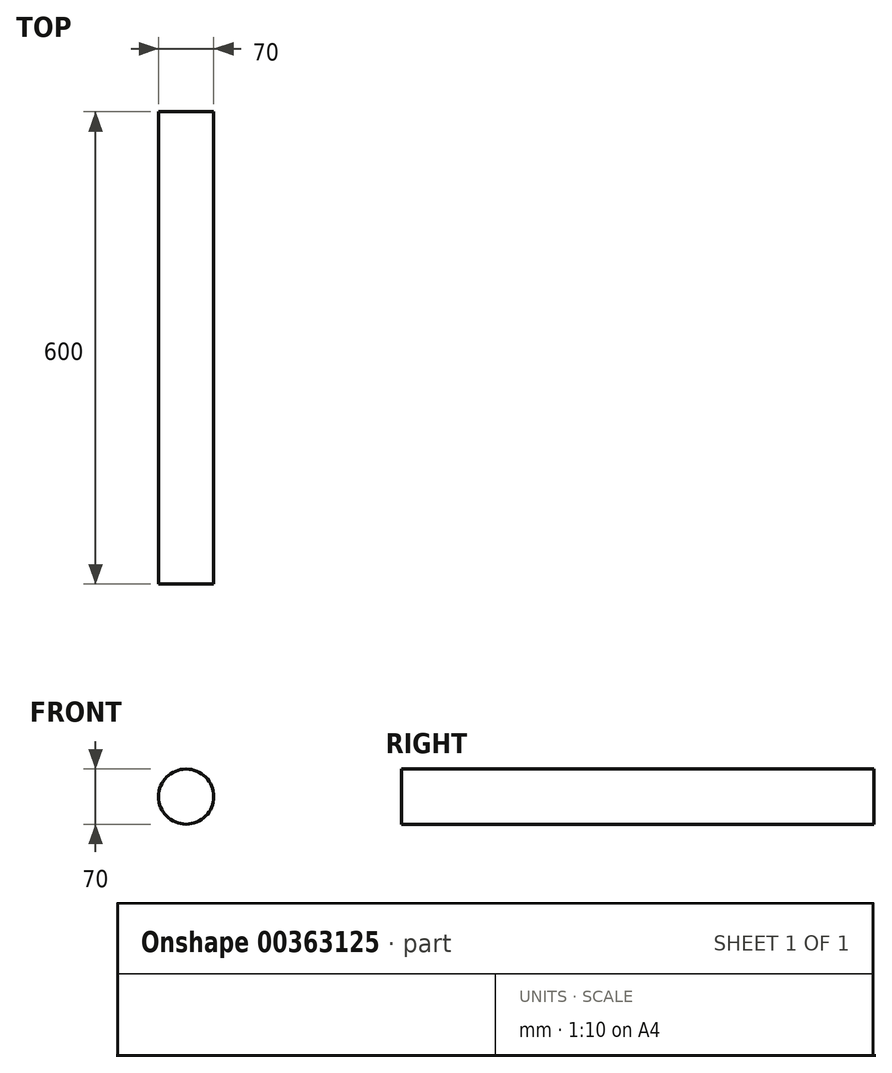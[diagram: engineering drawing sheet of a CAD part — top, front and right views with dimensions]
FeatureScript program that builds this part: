
annotation { "Feature Type Name" : "Feature", "Feature Type Description" : "" }
export const myFeature = defineFeature(function(context is Context, id is Id, definition is map)
    precondition{}
    {
        {
            var Q0;
            Q0=qCreatedBy(makeId("Front.planeOp"),FACE);
            var sketch = newSketch(context, id + "F0", { "sketchPlane" : qUnion([Q0])});
            skCircle(sketch, "E0", {"center": v(0, 0) * mm, "radius": 35 * mm});
            skSolve(sketch);
        }
        {
            var Q0;
            Q0 = qSketchRegion(id + "F0", true);
            extrude(context, id + "F1", {"entities" : qUnion([Q0]), "depth" : 600 * mm});
        }
    });
